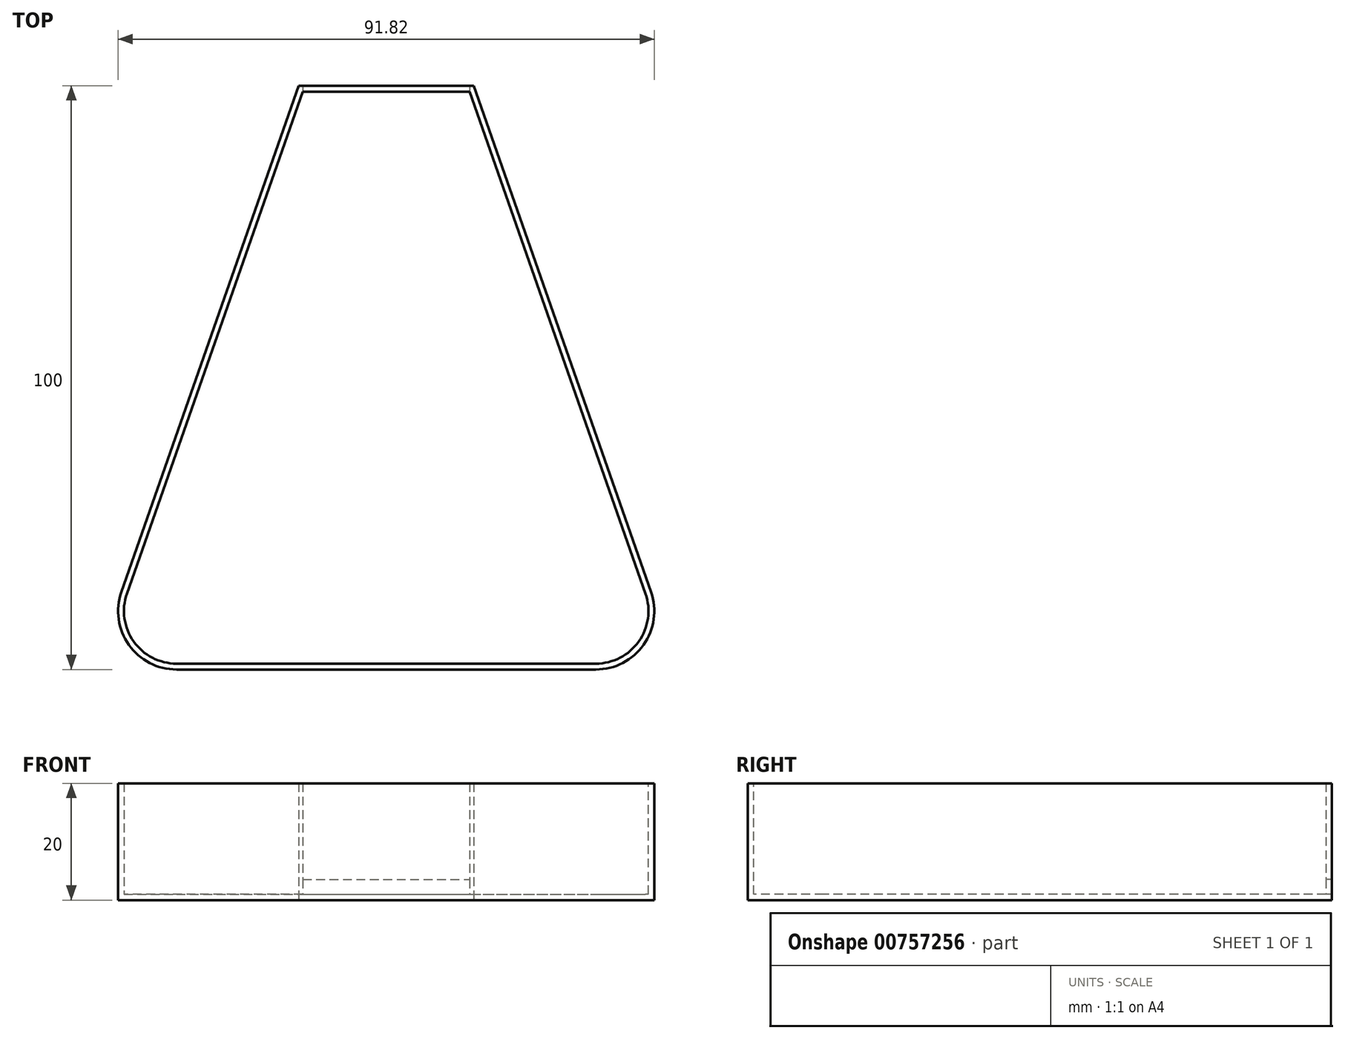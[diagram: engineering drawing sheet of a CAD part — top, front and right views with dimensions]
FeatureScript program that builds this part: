
annotation { "Feature Type Name" : "Feature", "Feature Type Description" : "" }
export const myFeature = defineFeature(function(context is Context, id is Id, definition is map)
    precondition{}
    {
        {
            var Q0;
            Q0=qCreatedBy(makeId("Top.planeOp"),FACE);
            var sketch = newSketch(context, id + "F0", { "sketchPlane" : qUnion([Q0])});
            skLineSegment(sketch, "E0.bottom", {"start": v(50, -50) * mm, "end": v(-50, -50) * mm, "construction": true});
            skLineSegment(sketch, "E0.top", {"start": v(50, 50) * mm, "end": v(-50, 50) * mm, "construction": true});
            skLineSegment(sketch, "E0.left", {"start": v(50, -50) * mm, "end": v(50, 50) * mm, "construction": true});
            skLineSegment(sketch, "E0.right", {"start": v(-50, -50) * mm, "end": v(-50, 50) * mm, "construction": true});
            skPoint(sketch, "E0.middle", {"position": v(0, 0) * mm});
            skLineSegment(sketch, "E1", {"start": v(-50, -50) * mm, "end": v(50, -50) * mm});
            skLineSegment(sketch, "E2.bottom", {"start": v(15, 45) * mm, "end": v(-15, 45) * mm, "construction": true});
            skLineSegment(sketch, "E2.top", {"start": v(15, 55) * mm, "end": v(-15, 55) * mm, "construction": true});
            skLineSegment(sketch, "E2.left", {"start": v(15, 45) * mm, "end": v(15, 55) * mm, "construction": true});
            skLineSegment(sketch, "E2.right", {"start": v(-15, 45) * mm, "end": v(-15, 55) * mm, "construction": true});
            skPoint(sketch, "E2.middle", {"position": v(0, 50) * mm});
            skLineSegment(sketch, "E3", {"start": v(-15, 50) * mm, "end": v(-50, -50) * mm});
            skLineSegment(sketch, "E4", {"start": v(15, 50) * mm, "end": v(50, -50) * mm});
            skLineSegment(sketch, "E5", {"start": v(-15, 50) * mm, "end": v(15, 50) * mm});
            skSolve(sketch);
        }
        {
            var Q0;
            Q0=makeQuery(id+"F0.imprint","IMPRINT",FACE,{"disambiguationData":[TD([[makeQuery(id+"F0.imprint","IMPRINT",EDGE,{"derivedFrom":sQuery(id+"F0.wireOp",EDGE,"E1")}),1.0]])]});
            extrude(context, id + "F1", {"entities" : qUnion([Q0]), "depth" : 20 * mm, "offsetDistance" : 25 * mm});
        }
        {
            var Q0;
            Q0=makeQuery(id+"F1.opExtrude","SWEPT_EDGE",EDGE,{"disambiguationData":[OSD([sQuery(id+"F0.wireOp",EDGE,"E1"),sQuery(id+"F0.wireOp",EDGE,"E3")])]});
            var Q1;
            Q1=makeQuery(id+"F1.opExtrude","SWEPT_EDGE",EDGE,{"disambiguationData":[OSD([sQuery(id+"F0.wireOp",EDGE,"E1"),sQuery(id+"F0.wireOp",EDGE,"E4")])]});
            fillet(context, id + "F2", {"entities" : qUnion([Q0, Q1]), "tangentPropagation" : true, "radius" : 10 * mm, "defaultsChanged" : true, "vertexSettings" : [], "allowEdgeOverflow" : false});
        }
        {
            var Q0;
            Q0=makeQuery(id+"F1.opExtrude","CAP_FACE",FACE,{"disambiguationData":[OSD([sQuery(id+"F0.wireOp",EDGE,"E1"),sQuery(id+"F0.wireOp",EDGE,"E3"),sQuery(id+"F0.wireOp",EDGE,"E4"),sQuery(id+"F0.wireOp",EDGE,"E5")])],"isStart":false});
            shell(context, id + "F3", {"entities" : qUnion([Q0]), "thickness" : 1 * mm});
        }
        {
            var Q0;
            Q0=makeQuery(id+"F3.opShell","OFFSET_FACE",FACE,{"disambiguationData":[OSD([sQuery(id+"F0.wireOp",EDGE,"E5")])]});
            var sketch = newSketch(context, id + "F4", { "sketchPlane" : qUnion([Q0])});
            skLineSegment(sketch, "E6.bottom", {"start": v(-14.3, 1) * mm, "end": v(14.3, 1) * mm});
            skLineSegment(sketch, "E6.top", {"start": v(-14.3, 3.5) * mm, "end": v(14.3, 3.5) * mm});
            skLineSegment(sketch, "E6.left", {"start": v(-14.3, 1) * mm, "end": v(-14.3, 3.5) * mm});
            skLineSegment(sketch, "E6.right", {"start": v(14.3, 1) * mm, "end": v(14.3, 3.5) * mm});
            skSolve(sketch);
        }
        {
            var Q0;
            Q0=makeQuery(id+"F4.imprint","IMPRINT",FACE,{"disambiguationData":[TD([[makeQuery(id+"F4.imprint","IMPRINT",EDGE,{"derivedFrom":sQuery(id+"F4.wireOp",EDGE,"E6.bottom")}),1.0]])]});
            extrude(context, id + "F5", {"entities" : qUnion([Q0]), "operationType" : NewBodyOperationType.REMOVE, "endBound" : BoundingType.UP_TO_NEXT, "oppositeDirection" : true, "depth" : 25 * mm, "offsetDistance" : 25 * mm});
        }
    });
